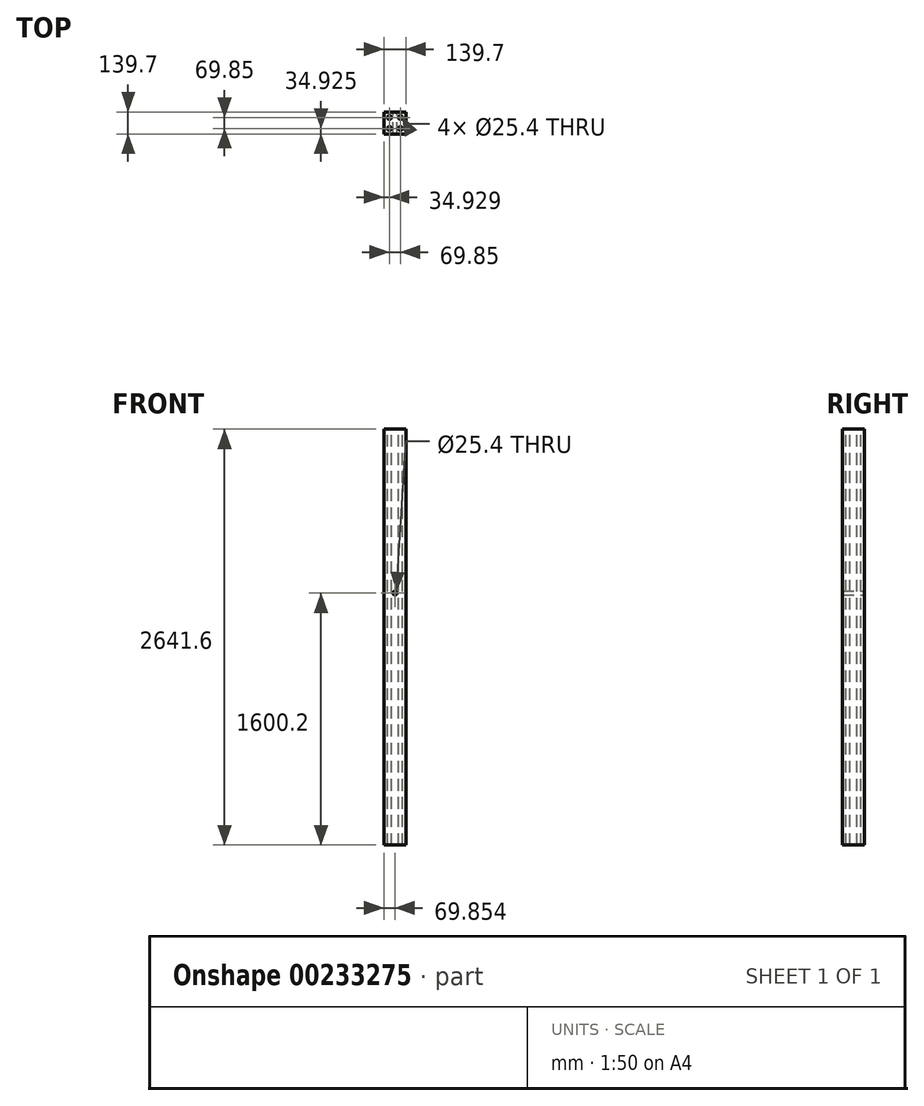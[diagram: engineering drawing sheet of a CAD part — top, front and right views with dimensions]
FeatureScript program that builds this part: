
annotation { "Feature Type Name" : "Feature", "Feature Type Description" : "" }
export const myFeature = defineFeature(function(context is Context, id is Id, definition is map)
    precondition{}
    {
        {
            var Q0;
            Q0=qCreatedBy(makeId("Front.planeOp"),FACE);
            var sketch = newSketch(context, id + "F0", { "sketchPlane" : qUnion([Q0])});
            skLineSegment(sketch, "E0.bottom", {"start": v(-82.68, 2615.23) * mm, "end": v(57.02, 2615.23) * mm});
            skLineSegment(sketch, "E0.top", {"start": v(-82.68, -26.37) * mm, "end": v(57.02, -26.37) * mm});
            skLineSegment(sketch, "E0.left", {"start": v(-82.68, 2615.23) * mm, "end": v(-82.68, -26.37) * mm});
            skLineSegment(sketch, "E0.right", {"start": v(57.02, 2615.23) * mm, "end": v(57.02, -26.37) * mm});
            skCircle(sketch, "E1", {"center": v(-12.83, 1573.83) * mm, "radius": 12.7 * mm});
            skSolve(sketch);
        }
        {
            var Q0;
            Q0=makeQuery(id+"F0.imprint","IMPRINT",FACE,{"disambiguationData":[TD([[makeQuery(id+"F0.imprint","IMPRINT",EDGE,{"derivedFrom":sQuery(id+"F0.wireOp",EDGE,"E0.bottom")}),-1.0]])]});
            extrude(context, id + "F1", {"entities" : qUnion([Q0]), "depth" : 139.7 * mm});
        }
        {
            var Q0;
            Q0=makeQuery(id+"F1.opExtrude","SWEPT_FACE",FACE,{"disambiguationData":[OSD([sQuery(id+"F0.wireOp",EDGE,"E0.bottom")])]});
            var sketch = newSketch(context, id + "F2", { "sketchPlane" : qUnion([Q0])});
            skCircle(sketch, "E2", {"center": v(-47.75, -34.93) * mm, "radius": 12.7 * mm});
            skCircle(sketch, "E3", {"center": v(22.1, -34.93) * mm, "radius": 12.7 * mm});
            skCircle(sketch, "E4", {"center": v(-47.75, -104.78) * mm, "radius": 12.7 * mm});
            skCircle(sketch, "E5", {"center": v(22.1, -104.78) * mm, "radius": 12.7 * mm});
            skSolve(sketch);
        }
        {
            var Q0;
            Q0=sQuery(id+"F2.wireOp",VERTEX,"E2.center");
            var Q1;
            Q1=sQuery(id+"F2.wireOp",VERTEX,"E3.center");
            var Q2;
            Q2=sQuery(id+"F2.wireOp",VERTEX,"E5.center");
            var Q3;
            Q3=sQuery(id+"F2.wireOp",VERTEX,"E4.center");
            var Q4;
            Q4=makeQuery(id+"F1.opExtrude","SWEPT_BODY",BODY,{"disambiguationData":[OSD([sQuery(id+"F0.wireOp",EDGE,"E0.bottom"),sQuery(id+"F0.wireOp",EDGE,"E0.top"),sQuery(id+"F0.wireOp",EDGE,"E0.left"),sQuery(id+"F0.wireOp",EDGE,"E0.right"),sQuery(id+"F0.wireOp",EDGE,"E1")])]});
            hole(context, id + "F3", {"style" : HoleStyle.SIMPLE, "endStyle" : HoleEndStyle.THROUGH, "holeDiameter" : 25.4 * mm, "tappedDepth" : 12.7 * mm, "tapClearance" : 3, "locations" : qUnion([Q0, Q1, Q2, Q3]), "scope" : qUnion([Q4])});
        }
    });
